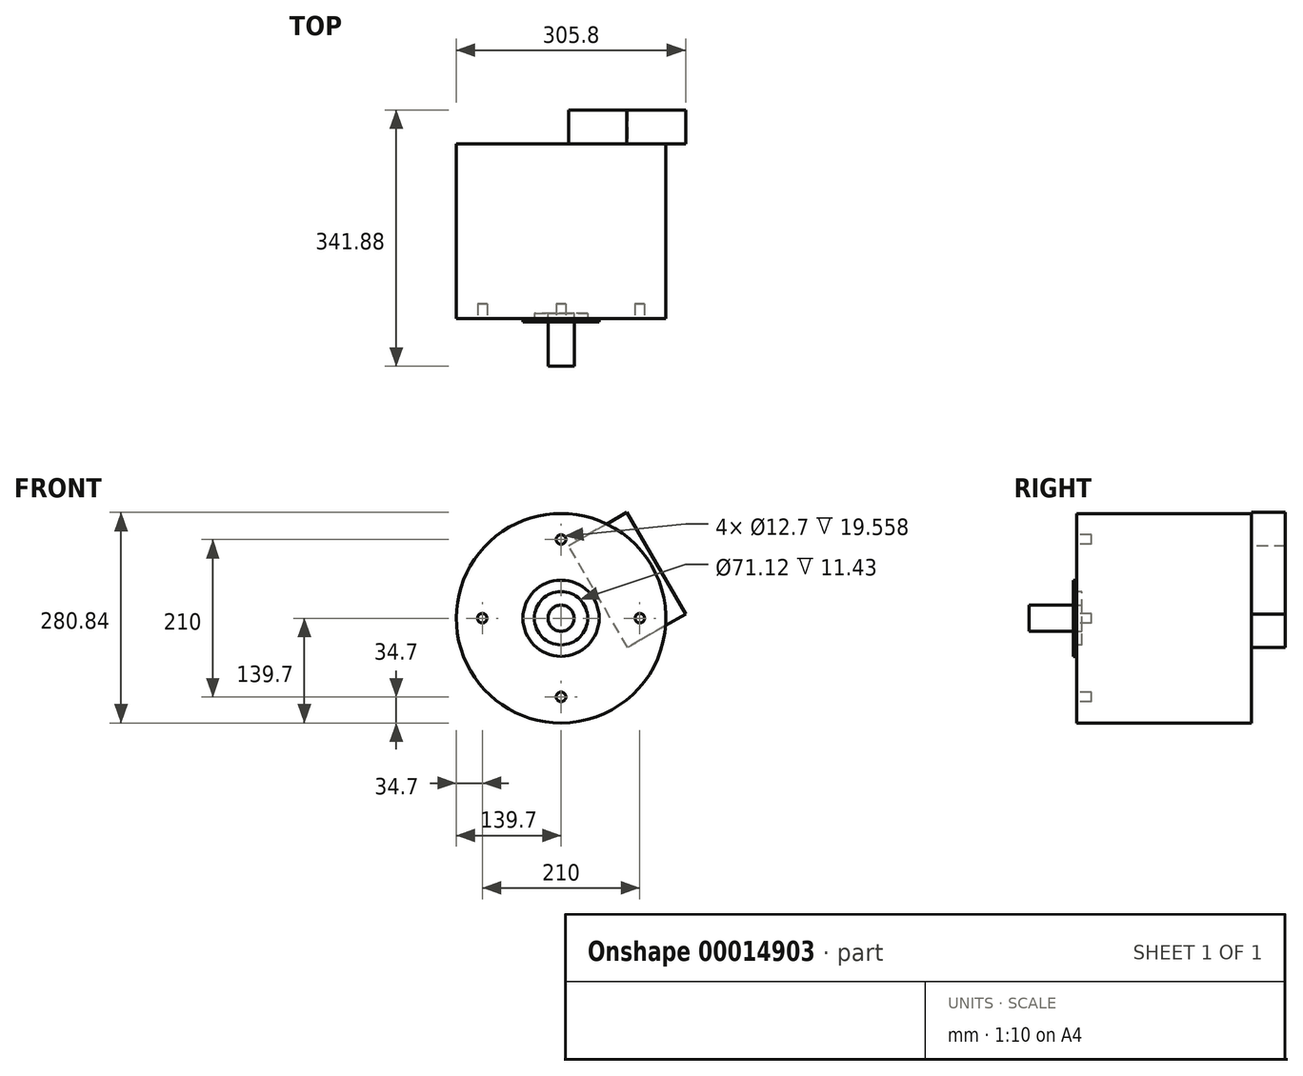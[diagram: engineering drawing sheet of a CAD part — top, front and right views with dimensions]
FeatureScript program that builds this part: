
annotation { "Feature Type Name" : "Feature", "Feature Type Description" : "" }
export const myFeature = defineFeature(function(context is Context, id is Id, definition is map)
    precondition{}
    {
        {
            var Q0;
            Q0=qCreatedBy(makeId("Front.planeOp"),FACE);
            var sketch = newSketch(context, id + "F0", { "sketchPlane" : qUnion([Q0])});
            skCircle(sketch, "E0", {"center": v(0, 0) * mm, "radius": 139.7 * mm});
            skSolve(sketch);
        }
        {
            var Q0;
            Q0 = qSketchRegion(id + "F0", true);
            extrude(context, id + "F1", {"entities" : qUnion([Q0]), "depth" : 233.17 * mm});
        }
        {
            var Q0;
            Q0=makeQuery(id+"F1.opExtrude","CAP_FACE",FACE,{"disambiguationData":[OSD([sQuery(id+"F0.wireOp",EDGE,"E0")])],"isStart":false});
            var sketch = newSketch(context, id + "F2", { "sketchPlane" : qUnion([Q0])});
            skCircle(sketch, "E1", {"center": v(0, 0) * mm, "radius": 50.8 * mm});
            skSolve(sketch);
        }
        {
            var Q0;
            Q0 = qSketchRegion(id + "F2", true);
            extrude(context, id + "F3", {"entities" : qUnion([Q0]), "operationType" : NewBodyOperationType.ADD, "depth" : 4.32 * mm});
        }
        {
            var Q0;
            Q0=makeQuery(id+"F3.opExtrude","CAP_FACE",FACE,{"disambiguationData":[OSD([sQuery(id+"F2.wireOp",EDGE,"E1")])],"isStart":false});
            var sketch = newSketch(context, id + "F4", { "sketchPlane" : qUnion([Q0])});
            skCircle(sketch, "E2", {"center": v(0, 0) * mm, "radius": 35.56 * mm});
            skSolve(sketch);
        }
        {
            var Q0;
            Q0 = qSketchRegion(id + "F4", true);
            extrude(context, id + "F5", {"entities" : qUnion([Q0]), "operationType" : NewBodyOperationType.REMOVE, "oppositeDirection" : true, "depth" : 11.43 * mm});
        }
        {
            var Q0;
            Q0=makeQuery(id+"F5.boolean.opBoolean","COPY",FACE,{"derivedFrom":makeQuery(id+"F5.opExtrude","CAP_FACE",FACE,{"disambiguationData":[OSD([sQuery(id+"F4.wireOp",EDGE,"E2")])],"isStart":false})});
            var sketch = newSketch(context, id + "F6", { "sketchPlane" : qUnion([Q0])});
            skCircle(sketch, "E3", {"center": v(0, 0) * mm, "radius": 17.46 * mm});
            skSolve(sketch);
        }
        {
            var Q0;
            Q0 = qSketchRegion(id + "F6", true);
            extrude(context, id + "F7", {"entities" : qUnion([Q0]), "operationType" : NewBodyOperationType.ADD, "depth" : 70.61 * mm});
        }
        {
            var Q0;
            Q0=makeQuery(id+"F1.opExtrude","CAP_FACE",FACE,{"disambiguationData":[OSD([sQuery(id+"F0.wireOp",EDGE,"E0")])],"isStart":false});
            var sketch = newSketch(context, id + "F8", { "sketchPlane" : qUnion([Q0])});
            skCircle(sketch, "E4", {"center": v(0, 0) * mm, "radius": 105 * mm, "construction": true});
            skLineSegment(sketch, "E5", {"start": v(0, 0) * mm, "end": v(0, 105) * mm, "construction": true});
            skLineSegment(sketch, "E6", {"start": v(0, 0) * mm, "end": v(-105, 0) * mm, "construction": true});
            skLineSegment(sketch, "E7", {"start": v(0, 0) * mm, "end": v(0, -105) * mm, "construction": true});
            skLineSegment(sketch, "E8", {"start": v(0, 0) * mm, "end": v(105, 0) * mm, "construction": true});
            skCircle(sketch, "E9", {"center": v(0, 105) * mm, "radius": 6.35 * mm});
            skCircle(sketch, "E10", {"center": v(-105, 0) * mm, "radius": 6.35 * mm});
            skCircle(sketch, "E11", {"center": v(0, -105) * mm, "radius": 6.35 * mm});
            skCircle(sketch, "E12", {"center": v(105, 0) * mm, "radius": 6.35 * mm});
            skSolve(sketch);
        }
        {
            var Q0;
            Q0 = qSketchRegion(id + "F8", true);
            extrude(context, id + "F9", {"entities" : qUnion([Q0]), "operationType" : NewBodyOperationType.REMOVE, "oppositeDirection" : true, "depth" : 19.56 * mm});
        }
        {
            var Q0;
            Q0=makeQuery(id+"F1.opExtrude","CAP_FACE",FACE,{"disambiguationData":[OSD([sQuery(id+"F0.wireOp",EDGE,"E0")])],"isStart":true});
            var sketch = newSketch(context, id + "F10", { "sketchPlane" : qUnion([Q0])});
            skLineSegment(sketch, "E13", {"start": v(0, 0) * mm, "end": v(69.85, 120.98) * mm, "construction": true});
            skLineSegment(sketch, "E14.bottom", {"start": v(-166.1, 5.42) * mm, "end": v(-87.74, 141.14) * mm});
            skLineSegment(sketch, "E14.top", {"start": v(-88.67, -39.29) * mm, "end": v(-10.31, 96.44) * mm});
            skLineSegment(sketch, "E14.left", {"start": v(-166.1, 5.42) * mm, "end": v(-88.67, -39.29) * mm});
            skLineSegment(sketch, "E14.right", {"start": v(-87.74, 141.14) * mm, "end": v(-10.31, 96.44) * mm});
            skLineSegment(sketch, "E15", {"start": v(0, 0) * mm, "end": v(-120.98, 69.85) * mm, "construction": true});
            skSolve(sketch);
        }
        {
            var Q0;
            Q0 = qSketchRegion(id + "F10", true);
            extrude(context, id + "F11", {"entities" : qUnion([Q0]), "operationType" : NewBodyOperationType.ADD, "depth" : 45.2 * mm});
        }
    });
